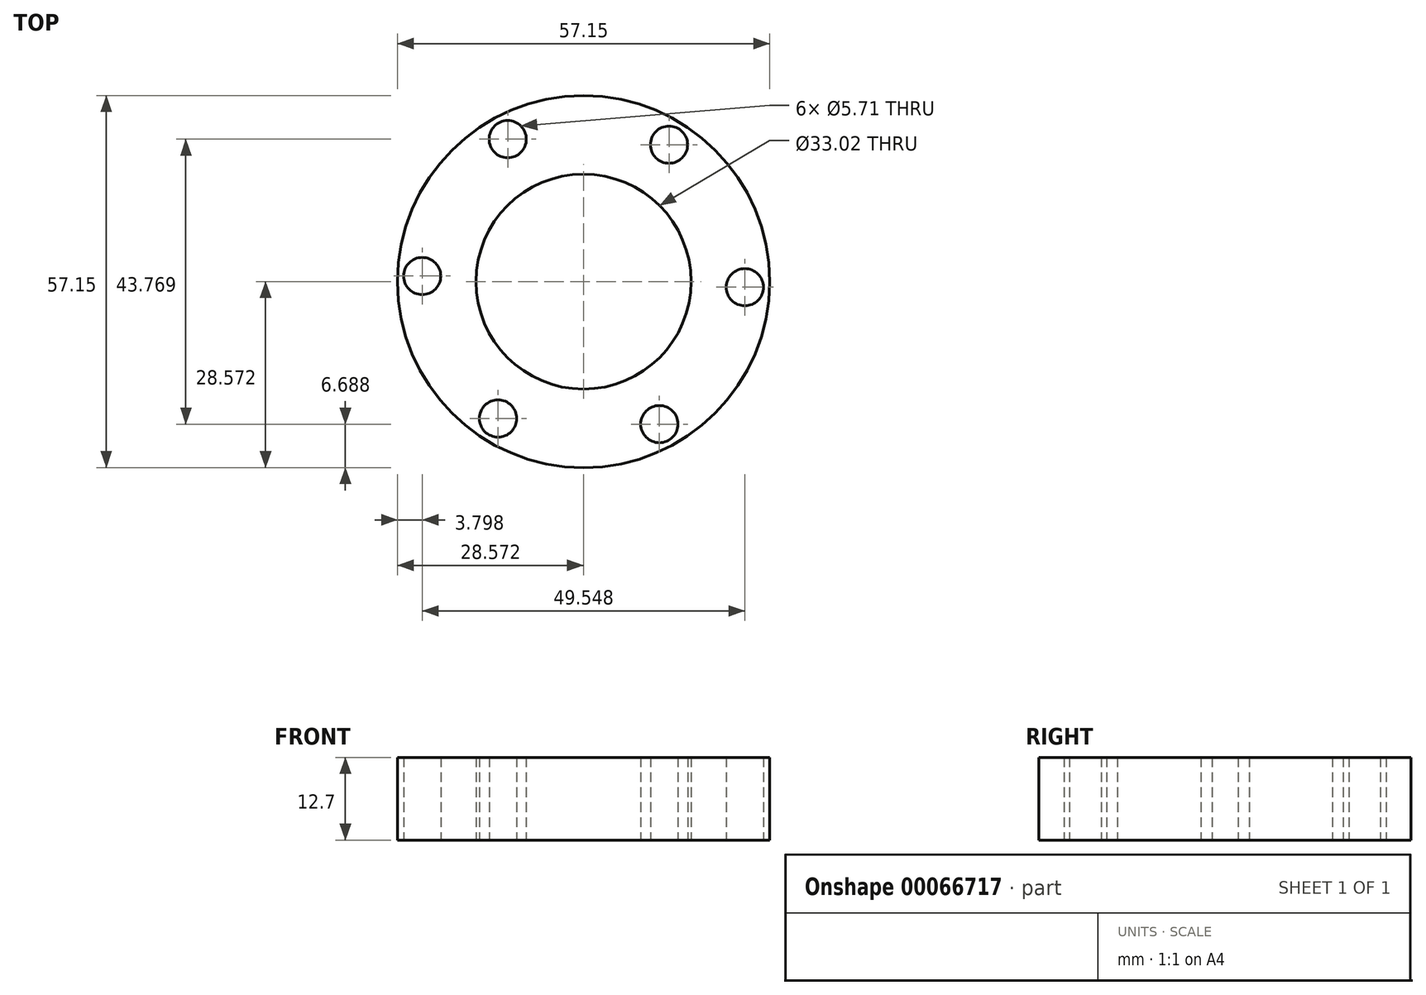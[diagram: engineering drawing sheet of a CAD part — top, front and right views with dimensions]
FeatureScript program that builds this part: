
annotation { "Feature Type Name" : "Feature", "Feature Type Description" : "" }
export const myFeature = defineFeature(function(context is Context, id is Id, definition is map)
    precondition{}
    {
        {
            var Q0;
            Q0=qCreatedBy(makeId("Top.planeOp"),FACE);
            var sketch = newSketch(context, id + "F0", { "sketchPlane" : qUnion([Q0])});
            skCircle(sketch, "E0", {"center": v(-112.35, -25.49) * mm, "radius": 28.58 * mm});
            skCircle(sketch, "E1", {"center": v(-112.35, -25.49) * mm, "radius": 16.51 * mm});
            skCircle(sketch, "E2", {"center": v(-137.12, -24.63) * mm, "radius": 2.86 * mm});
            skCircle(sketch, "E3.1.0", {"center": v(-125.48, -46.51) * mm, "radius": 2.86 * mm});
            skCircle(sketch, "E3.2.0", {"center": v(-100.7, -47.37) * mm, "radius": 2.86 * mm});
            skCircle(sketch, "E3.3.0", {"center": v(-87.57, -26.35) * mm, "radius": 2.86 * mm});
            skCircle(sketch, "E3.4.0", {"center": v(-99.22, -4.46) * mm, "radius": 2.86 * mm});
            skCircle(sketch, "E3.5.0", {"center": v(-124, -3.6) * mm, "radius": 2.86 * mm});
            skSolve(sketch);
        }
        {
            var Q0;
            Q0=makeQuery(id+"F0.imprint","IMPRINT",FACE,{"disambiguationData":[TD([[makeQuery(id+"F0.imprint","IMPRINT",EDGE,{"derivedFrom":sQuery(id+"F0.wireOp",EDGE,"E0")}),1.0]])]});
            extrude(context, id + "F1", {"entities" : qUnion([Q0]), "depth" : 12.7 * mm});
        }
    });
